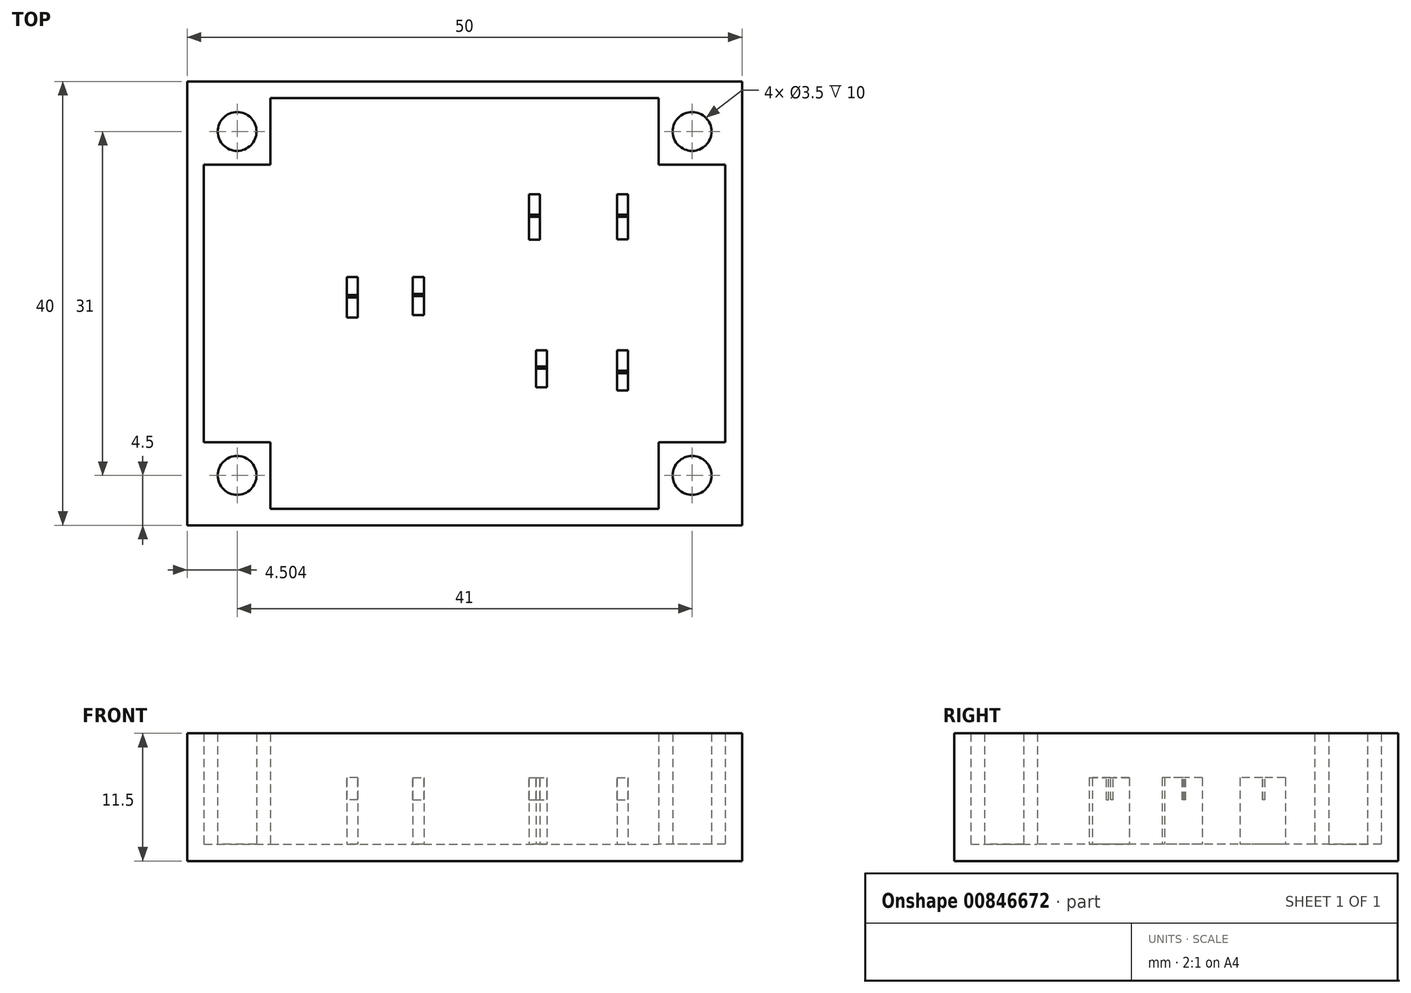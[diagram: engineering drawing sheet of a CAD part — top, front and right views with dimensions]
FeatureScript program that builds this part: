
annotation { "Feature Type Name" : "Feature", "Feature Type Description" : "" }
export const myFeature = defineFeature(function(context is Context, id is Id, definition is map)
    precondition{}
    {
        {
            var Q0;
            Q0=qCreatedBy(makeId("Top.planeOp"),FACE);
            var sketch = newSketch(context, id + "F0", { "sketchPlane" : qUnion([Q0])});
            skLineSegment(sketch, "E0.bottom", {"start": v(-23.35, 9.23) * mm, "end": v(26.65, 9.23) * mm});
            skLineSegment(sketch, "E0.top", {"start": v(-23.35, -30.77) * mm, "end": v(26.65, -30.77) * mm});
            skLineSegment(sketch, "E0.left", {"start": v(-23.35, 9.23) * mm, "end": v(-23.35, -30.77) * mm});
            skLineSegment(sketch, "E0.right", {"start": v(26.65, 9.23) * mm, "end": v(26.65, -30.77) * mm});
            skSolve(sketch);
        }
        {
            var Q0;
            Q0=makeQuery(id+"F0.imprint","IMPRINT",FACE,{"disambiguationData":[TD([[makeQuery(id+"F0.imprint","IMPRINT",EDGE,{"derivedFrom":sQuery(id+"F0.wireOp",EDGE,"E0.bottom")}),-1.0]])]});
            extrude(context, id + "F1", {"entities" : qUnion([Q0]), "depth" : 1.5 * mm, "offsetDistance" : 25 * mm});
        }
        {
            var Q0;
            Q0=makeQuery(id+"F1.opExtrude","CAP_FACE",FACE,{"disambiguationData":[OSD([sQuery(id+"F0.wireOp",EDGE,"E0.bottom"),sQuery(id+"F0.wireOp",EDGE,"E0.top"),sQuery(id+"F0.wireOp",EDGE,"E0.left"),sQuery(id+"F0.wireOp",EDGE,"E0.right")])],"isStart":false});
            var sketch = newSketch(context, id + "F2", { "sketchPlane" : qUnion([Q0])});
            skLineSegment(sketch, "E1.bottom", {"start": v(-23.35, 9.23) * mm, "end": v(26.65, 9.23) * mm});
            skLineSegment(sketch, "E1.top", {"start": v(-23.35, -30.77) * mm, "end": v(26.65, -30.77) * mm});
            skLineSegment(sketch, "E1.left", {"start": v(-23.35, 9.23) * mm, "end": v(-23.35, -30.77) * mm});
            skLineSegment(sketch, "E1.right", {"start": v(26.65, 9.23) * mm, "end": v(26.65, -30.77) * mm});
            skLineSegment(sketch, "E2.bottom", {"start": v(-21.85, 7.73) * mm, "end": v(25.15, 7.73) * mm});
            skLineSegment(sketch, "E2.top", {"start": v(-21.85, -29.27) * mm, "end": v(25.15, -29.27) * mm});
            skLineSegment(sketch, "E2.left", {"start": v(-21.85, 7.73) * mm, "end": v(-21.85, -29.27) * mm});
            skLineSegment(sketch, "E2.right", {"start": v(25.15, 7.73) * mm, "end": v(25.15, -29.27) * mm});
            skLineSegment(sketch, "E3.bottom", {"start": v(19.15, 7.73) * mm, "end": v(25.15, 7.73) * mm});
            skLineSegment(sketch, "E3.top", {"start": v(19.15, 1.73) * mm, "end": v(25.15, 1.73) * mm});
            skLineSegment(sketch, "E3.left", {"start": v(19.15, 7.73) * mm, "end": v(19.15, 1.73) * mm});
            skLineSegment(sketch, "E3.right", {"start": v(25.15, 7.73) * mm, "end": v(25.15, 1.73) * mm});
            skCircle(sketch, "E4", {"center": v(22.29, 4.73) * mm, "radius": 1.75 * mm});
            skPoint(sketch, "E4.centerSnap0", {"position": v(25.15, 4.73) * mm});
            skSolve(sketch);
        }
        {
            var Q0;
            Q0 = qSketchRegion(id + "F2", true);
            extrude(context, id + "F3", {"entities" : qUnion([Q0]), "operationType" : NewBodyOperationType.ADD, "depth" : 10 * mm, "offsetDistance" : 25 * mm});
        }
        {
            var Q0;
            Q0=makeQuery(id+"F1.opExtrude","CAP_FACE",FACE,{"disambiguationData":[OSD([sQuery(id+"F0.wireOp",EDGE,"E0.bottom"),sQuery(id+"F0.wireOp",EDGE,"E0.top"),sQuery(id+"F0.wireOp",EDGE,"E0.left"),sQuery(id+"F0.wireOp",EDGE,"E0.right")])],"isStart":false});
            var sketch = newSketch(context, id + "F4", { "sketchPlane" : qUnion([Q0])});
            skLineSegment(sketch, "E5.bottom", {"start": v(-21.85, 7.73) * mm, "end": v(-15.85, 7.73) * mm});
            skLineSegment(sketch, "E5.top", {"start": v(-21.85, 1.73) * mm, "end": v(-15.85, 1.73) * mm});
            skLineSegment(sketch, "E5.left", {"start": v(-21.85, 7.73) * mm, "end": v(-21.85, 1.73) * mm});
            skLineSegment(sketch, "E5.right", {"start": v(-15.85, 7.73) * mm, "end": v(-15.85, 1.73) * mm});
            skLineSegment(sketch, "E6", {"start": v(-21.85, 1.73) * mm, "end": v(-15.85, 7.73) * mm});
            skLineSegment(sketch, "E7", {"start": v(-21.85, 7.73) * mm, "end": v(-15.85, 1.73) * mm});
            skCircle(sketch, "E8", {"center": v(-18.85, 4.73) * mm, "radius": 1.75 * mm});
            skSolve(sketch);
        }
        {
            var Q0;
            Q0 = qSketchRegion(id + "F4", true);
            extrude(context, id + "F5", {"entities" : qUnion([Q0]), "operationType" : NewBodyOperationType.ADD, "depth" : 10 * mm, "offsetDistance" : 25 * mm});
        }
        {
            var Q0;
            Q0=makeQuery(id+"F5.boolean.opBoolean","SPLIT",FACE,{"disambiguationData":[TD([makeQuery(id+"F3.opExtrude","SWEPT_FACE",FACE,{"disambiguationData":[OSD([sQuery(id+"F2.wireOp",EDGE,"E2.top")])]})])],"derivedFrom":makeQuery(id+"F1.opExtrude","CAP_FACE",FACE,{"disambiguationData":[OSD([sQuery(id+"F0.wireOp",EDGE,"E0.bottom"),sQuery(id+"F0.wireOp",EDGE,"E0.top"),sQuery(id+"F0.wireOp",EDGE,"E0.left"),sQuery(id+"F0.wireOp",EDGE,"E0.right")])],"isStart":false})});
            var sketch = newSketch(context, id + "F6", { "sketchPlane" : qUnion([Q0])});
            skLineSegment(sketch, "E9.bottom", {"start": v(-21.85, -29.27) * mm, "end": v(-15.85, -29.27) * mm});
            skLineSegment(sketch, "E9.top", {"start": v(-21.85, -23.27) * mm, "end": v(-15.85, -23.27) * mm});
            skLineSegment(sketch, "E9.left", {"start": v(-21.85, -29.27) * mm, "end": v(-21.85, -23.27) * mm});
            skLineSegment(sketch, "E9.right", {"start": v(-15.85, -29.27) * mm, "end": v(-15.85, -23.27) * mm});
            skLineSegment(sketch, "E10", {"start": v(-21.85, -29.27) * mm, "end": v(-15.85, -23.27) * mm});
            skLineSegment(sketch, "E11", {"start": v(-21.85, -23.27) * mm, "end": v(-15.85, -29.27) * mm});
            skCircle(sketch, "E12", {"center": v(-18.85, -26.27) * mm, "radius": 1.75 * mm});
            skSolve(sketch);
        }
        {
            var Q0;
            Q0 = qSketchRegion(id + "F6", true);
            extrude(context, id + "F7", {"entities" : qUnion([Q0]), "operationType" : NewBodyOperationType.ADD, "depth" : 10 * mm, "offsetDistance" : 25 * mm});
        }
        {
            var Q0;
            {var subQ3=makeQuery(id+"F3.opExtrude","SWEPT_FACE",FACE,{"disambiguationData":[OSD([sQuery(id+"F2.wireOp",EDGE,"E2.top")])]});Q0=makeQuery(id+"F7.boolean.opBoolean","SPLIT",FACE,{"disambiguationData":[TD([subQ3])],"derivedFrom":makeQuery(id+"F5.boolean.opBoolean","SPLIT",FACE,{"disambiguationData":[TD([subQ3])],"derivedFrom":makeQuery(id+"F1.opExtrude","CAP_FACE",FACE,{"disambiguationData":[OSD([sQuery(id+"F0.wireOp",EDGE,"E0.bottom"),sQuery(id+"F0.wireOp",EDGE,"E0.top"),sQuery(id+"F0.wireOp",EDGE,"E0.left"),sQuery(id+"F0.wireOp",EDGE,"E0.right")])],"isStart":false})})});}
            var sketch = newSketch(context, id + "F8", { "sketchPlane" : qUnion([Q0])});
            skLineSegment(sketch, "E13.bottom", {"start": v(25.15, 7.73) * mm, "end": v(19.15, 7.73) * mm});
            skLineSegment(sketch, "E13.top", {"start": v(25.15, 1.73) * mm, "end": v(19.15, 1.73) * mm});
            skLineSegment(sketch, "E13.left", {"start": v(25.15, 7.73) * mm, "end": v(25.15, 1.73) * mm});
            skLineSegment(sketch, "E13.right", {"start": v(19.15, 7.73) * mm, "end": v(19.15, 1.73) * mm});
            skLineSegment(sketch, "E14", {"start": v(19.15, 1.73) * mm, "end": v(25.15, 7.73) * mm});
            skLineSegment(sketch, "E15", {"start": v(19.15, 7.73) * mm, "end": v(25.15, 1.73) * mm});
            skCircle(sketch, "E16", {"center": v(22.15, 4.73) * mm, "radius": 1.75 * mm});
            skSolve(sketch);
        }
        {
            var Q0;
            Q0 = qSketchRegion(id + "F8", true);
            extrude(context, id + "F9", {"entities" : qUnion([Q0]), "operationType" : NewBodyOperationType.ADD, "depth" : 10 * mm, "offsetDistance" : 25 * mm});
        }
        {
            var Q0;
            {var subQ3=makeQuery(id+"F3.opExtrude","SWEPT_FACE",FACE,{"disambiguationData":[OSD([sQuery(id+"F2.wireOp",EDGE,"E2.top")])]});Q0=makeQuery(id+"F9.boolean.opBoolean","SPLIT",FACE,{"disambiguationData":[TD([subQ3])],"derivedFrom":makeQuery(id+"F7.boolean.opBoolean","SPLIT",FACE,{"disambiguationData":[TD([subQ3])],"derivedFrom":makeQuery(id+"F5.boolean.opBoolean","SPLIT",FACE,{"disambiguationData":[TD([subQ3])],"derivedFrom":makeQuery(id+"F1.opExtrude","CAP_FACE",FACE,{"disambiguationData":[OSD([sQuery(id+"F0.wireOp",EDGE,"E0.bottom"),sQuery(id+"F0.wireOp",EDGE,"E0.top"),sQuery(id+"F0.wireOp",EDGE,"E0.left"),sQuery(id+"F0.wireOp",EDGE,"E0.right")])],"isStart":false})})})});}
            var sketch = newSketch(context, id + "F10", { "sketchPlane" : qUnion([Q0])});
            skLineSegment(sketch, "E17.bottom", {"start": v(25.15, -29.27) * mm, "end": v(19.15, -29.27) * mm});
            skLineSegment(sketch, "E17.top", {"start": v(25.15, -23.27) * mm, "end": v(19.15, -23.27) * mm});
            skLineSegment(sketch, "E17.left", {"start": v(25.15, -29.27) * mm, "end": v(25.15, -23.27) * mm});
            skLineSegment(sketch, "E17.right", {"start": v(19.15, -29.27) * mm, "end": v(19.15, -23.27) * mm});
            skLineSegment(sketch, "E18", {"start": v(19.15, -29.27) * mm, "end": v(25.15, -23.27) * mm});
            skLineSegment(sketch, "E19", {"start": v(19.15, -23.27) * mm, "end": v(25.15, -29.27) * mm});
            skCircle(sketch, "E20", {"center": v(22.15, -26.27) * mm, "radius": 1.75 * mm});
            skSolve(sketch);
        }
        {
            var Q0;
            Q0 = qSketchRegion(id + "F10", true);
            extrude(context, id + "F11", {"entities" : qUnion([Q0]), "operationType" : NewBodyOperationType.ADD, "depth" : 10 * mm, "offsetDistance" : 25 * mm});
        }
        {
            var Q0;
            Q0=makeQuery(id+"F1.opExtrude","SWEPT_BODY",BODY,{"disambiguationData":[OSD([sQuery(id+"F0.wireOp",EDGE,"E0.bottom"),sQuery(id+"F0.wireOp",EDGE,"E0.top"),sQuery(id+"F0.wireOp",EDGE,"E0.left"),sQuery(id+"F0.wireOp",EDGE,"E0.right")])]});
            transform(context, id + "F12", {"entities" : qUnion([Q0]), "transformType" : TransformType.TRANSLATION_3D, "dx" : 0 * mm, "dy" : 0 * mm, "dz" : 0 * mm, "makeCopy" : true});
        }
        {
            var Q0;
            Q0=makeQuery(id+"F12.opPattern","COPY",BODY,{"derivedFrom":makeQuery(id+"F1.opExtrude","SWEPT_BODY",BODY,{"disambiguationData":[OSD([sQuery(id+"F0.wireOp",EDGE,"E0.bottom"),sQuery(id+"F0.wireOp",EDGE,"E0.top"),sQuery(id+"F0.wireOp",EDGE,"E0.left"),sQuery(id+"F0.wireOp",EDGE,"E0.right")])]}),"instanceName":"1"});
            deleteBodies(context, id + "F13", {"entities" : qUnion([Q0])});
        }
        {
            var Q0;
            {var subQ6=makeQuery(id+"F3.opExtrude","SWEPT_FACE",FACE,{"disambiguationData":[OSD([sQuery(id+"F2.wireOp",EDGE,"E2.top")])]});Q0=makeQuery(id+"F11.boolean.opBoolean","SPLIT",FACE,{"disambiguationData":[TD([subQ6])],"derivedFrom":makeQuery(id+"F9.boolean.opBoolean","SPLIT",FACE,{"disambiguationData":[TD([subQ6])],"derivedFrom":makeQuery(id+"F7.boolean.opBoolean","SPLIT",FACE,{"disambiguationData":[TD([subQ6])],"derivedFrom":makeQuery(id+"F5.boolean.opBoolean","SPLIT",FACE,{"disambiguationData":[TD([subQ6])],"derivedFrom":makeQuery(id+"F1.opExtrude","CAP_FACE",FACE,{"disambiguationData":[OSD([sQuery(id+"F0.wireOp",EDGE,"E0.bottom"),sQuery(id+"F0.wireOp",EDGE,"E0.top"),sQuery(id+"F0.wireOp",EDGE,"E0.left"),sQuery(id+"F0.wireOp",EDGE,"E0.right")])],"isStart":false})})})})});}
            var sketch = newSketch(context, id + "F14", { "sketchPlane" : qUnion([Q0])});
            skLineSegment(sketch, "E21.bottom", {"start": v(16.38, -0.92) * mm, "end": v(15.38, -0.92) * mm});
            skLineSegment(sketch, "E21.top", {"start": v(16.38, -5) * mm, "end": v(15.38, -5) * mm});
            skLineSegment(sketch, "E21.left", {"start": v(16.38, -0.92) * mm, "end": v(16.38, -5) * mm});
            skLineSegment(sketch, "E21.right", {"start": v(15.38, -0.92) * mm, "end": v(15.38, -5) * mm});
            skSolve(sketch);
        }
        {
            var Q0;
            Q0 = qSketchRegion(id + "F14", true);
            extrude(context, id + "F15", {"entities" : qUnion([Q0]), "operationType" : NewBodyOperationType.ADD, "depth" : 6 * mm, "offsetDistance" : 25 * mm});
        }
        {
            var Q0;
            Q0=makeQuery(id+"F15.opExtrude","CAP_FACE",FACE,{"disambiguationData":[OSD([sQuery(id+"F14.wireOp",EDGE,"E21.bottom"),sQuery(id+"F14.wireOp",EDGE,"E21.top"),sQuery(id+"F14.wireOp",EDGE,"E21.left"),sQuery(id+"F14.wireOp",EDGE,"E21.right")])],"isStart":false});
            var sketch = newSketch(context, id + "F16", { "sketchPlane" : qUnion([Q0])});
            skLineSegment(sketch, "E22.bottom", {"start": v(15.38, -2.76) * mm, "end": v(16.38, -2.76) * mm});
            skLineSegment(sketch, "E22.top", {"start": v(15.38, -2.96) * mm, "end": v(16.38, -2.96) * mm});
            skLineSegment(sketch, "E22.left", {"start": v(15.38, -2.76) * mm, "end": v(15.38, -2.96) * mm});
            skLineSegment(sketch, "E22.right", {"start": v(16.38, -2.76) * mm, "end": v(16.38, -2.96) * mm});
            skSolve(sketch);
        }
        {
            var Q0;
            Q0 = qSketchRegion(id + "F16", true);
            extrude(context, id + "F17", {"entities" : qUnion([Q0]), "operationType" : NewBodyOperationType.REMOVE, "oppositeDirection" : true, "depth" : 2 * mm, "offsetDistance" : 25 * mm});
        }
        {
            var Q0;
            {var subQ6=makeQuery(id+"F3.opExtrude","SWEPT_FACE",FACE,{"disambiguationData":[OSD([sQuery(id+"F2.wireOp",EDGE,"E2.top")])]});Q0=makeQuery(id+"F11.boolean.opBoolean","SPLIT",FACE,{"disambiguationData":[TD([subQ6])],"derivedFrom":makeQuery(id+"F9.boolean.opBoolean","SPLIT",FACE,{"disambiguationData":[TD([subQ6])],"derivedFrom":makeQuery(id+"F7.boolean.opBoolean","SPLIT",FACE,{"disambiguationData":[TD([subQ6])],"derivedFrom":makeQuery(id+"F5.boolean.opBoolean","SPLIT",FACE,{"disambiguationData":[TD([subQ6])],"derivedFrom":makeQuery(id+"F1.opExtrude","CAP_FACE",FACE,{"disambiguationData":[OSD([sQuery(id+"F0.wireOp",EDGE,"E0.bottom"),sQuery(id+"F0.wireOp",EDGE,"E0.top"),sQuery(id+"F0.wireOp",EDGE,"E0.left"),sQuery(id+"F0.wireOp",EDGE,"E0.right")])],"isStart":false})})})})});}
            var sketch = newSketch(context, id + "F18", { "sketchPlane" : qUnion([Q0])});
            skLineSegment(sketch, "E23.bottom", {"start": v(15.38, -18.6) * mm, "end": v(16.38, -18.6) * mm});
            skLineSegment(sketch, "E23.top", {"start": v(15.38, -15) * mm, "end": v(16.38, -15) * mm});
            skLineSegment(sketch, "E23.left", {"start": v(15.38, -18.6) * mm, "end": v(15.38, -15) * mm});
            skLineSegment(sketch, "E23.right", {"start": v(16.38, -18.6) * mm, "end": v(16.38, -15) * mm});
            skSolve(sketch);
        }
        {
            var Q0;
            Q0 = qSketchRegion(id + "F18", true);
            extrude(context, id + "F19", {"entities" : qUnion([Q0]), "operationType" : NewBodyOperationType.ADD, "depth" : 6 * mm, "offsetDistance" : 25 * mm});
        }
        {
            var Q0;
            Q0=makeQuery(id+"F19.opExtrude","CAP_FACE",FACE,{"disambiguationData":[OSD([sQuery(id+"F18.wireOp",EDGE,"E23.bottom"),sQuery(id+"F18.wireOp",EDGE,"E23.top"),sQuery(id+"F18.wireOp",EDGE,"E23.left"),sQuery(id+"F18.wireOp",EDGE,"E23.right")])],"isStart":false});
            var sketch = newSketch(context, id + "F20", { "sketchPlane" : qUnion([Q0])});
            skLineSegment(sketch, "E24.bottom", {"start": v(15.38, -16.85) * mm, "end": v(16.38, -16.85) * mm});
            skLineSegment(sketch, "E24.top", {"start": v(15.38, -17.05) * mm, "end": v(16.38, -17.05) * mm});
            skLineSegment(sketch, "E24.left", {"start": v(15.38, -16.85) * mm, "end": v(15.38, -17.05) * mm});
            skLineSegment(sketch, "E24.right", {"start": v(16.38, -16.85) * mm, "end": v(16.38, -17.05) * mm});
            skSolve(sketch);
        }
        {
            var Q0;
            Q0 = qSketchRegion(id + "F20", true);
            extrude(context, id + "F21", {"entities" : qUnion([Q0]), "operationType" : NewBodyOperationType.REMOVE, "oppositeDirection" : true, "depth" : 2 * mm, "offsetDistance" : 25 * mm});
        }
        {
            var Q0;
            {var subQ6=makeQuery(id+"F3.opExtrude","SWEPT_FACE",FACE,{"disambiguationData":[OSD([sQuery(id+"F2.wireOp",EDGE,"E2.top")])]});Q0=makeQuery(id+"F11.boolean.opBoolean","SPLIT",FACE,{"disambiguationData":[TD([subQ6])],"derivedFrom":makeQuery(id+"F9.boolean.opBoolean","SPLIT",FACE,{"disambiguationData":[TD([subQ6])],"derivedFrom":makeQuery(id+"F7.boolean.opBoolean","SPLIT",FACE,{"disambiguationData":[TD([subQ6])],"derivedFrom":makeQuery(id+"F5.boolean.opBoolean","SPLIT",FACE,{"disambiguationData":[TD([subQ6])],"derivedFrom":makeQuery(id+"F1.opExtrude","CAP_FACE",FACE,{"disambiguationData":[OSD([sQuery(id+"F0.wireOp",EDGE,"E0.bottom"),sQuery(id+"F0.wireOp",EDGE,"E0.top"),sQuery(id+"F0.wireOp",EDGE,"E0.left"),sQuery(id+"F0.wireOp",EDGE,"E0.right")])],"isStart":false})})})})});}
            var sketch = newSketch(context, id + "F22", { "sketchPlane" : qUnion([Q0])});
            skLineSegment(sketch, "E25.bottom", {"start": v(8.46, -0.92) * mm, "end": v(7.46, -0.92) * mm});
            skLineSegment(sketch, "E25.top", {"start": v(8.46, -5.01) * mm, "end": v(7.46, -5.01) * mm});
            skLineSegment(sketch, "E25.left", {"start": v(8.46, -0.92) * mm, "end": v(8.46, -5.01) * mm});
            skLineSegment(sketch, "E25.right", {"start": v(7.46, -0.92) * mm, "end": v(7.46, -5.01) * mm});
            skSolve(sketch);
        }
        {
            var Q0;
            Q0 = qSketchRegion(id + "F22", true);
            extrude(context, id + "F23", {"entities" : qUnion([Q0]), "operationType" : NewBodyOperationType.ADD, "depth" : 6 * mm, "offsetDistance" : 25 * mm});
        }
        {
            var Q0;
            Q0=makeQuery(id+"F23.opExtrude","CAP_FACE",FACE,{"disambiguationData":[OSD([sQuery(id+"F22.wireOp",EDGE,"E25.bottom"),sQuery(id+"F22.wireOp",EDGE,"E25.top"),sQuery(id+"F22.wireOp",EDGE,"E25.left"),sQuery(id+"F22.wireOp",EDGE,"E25.right")])],"isStart":false});
            var sketch = newSketch(context, id + "F24", { "sketchPlane" : qUnion([Q0])});
            skLineSegment(sketch, "E26.bottom", {"start": v(7.46, -2.77) * mm, "end": v(8.46, -2.77) * mm});
            skLineSegment(sketch, "E26.top", {"start": v(7.46, -2.97) * mm, "end": v(8.46, -2.97) * mm});
            skLineSegment(sketch, "E26.left", {"start": v(7.46, -2.77) * mm, "end": v(7.46, -2.97) * mm});
            skLineSegment(sketch, "E26.right", {"start": v(8.46, -2.77) * mm, "end": v(8.46, -2.97) * mm});
            skSolve(sketch);
        }
        {
            var Q0;
            Q0 = qSketchRegion(id + "F24", true);
            extrude(context, id + "F25", {"entities" : qUnion([Q0]), "operationType" : NewBodyOperationType.REMOVE, "oppositeDirection" : true, "depth" : 2 * mm, "offsetDistance" : 25 * mm});
        }
        {
            var Q0;
            {var subQ6=makeQuery(id+"F3.opExtrude","SWEPT_FACE",FACE,{"disambiguationData":[OSD([sQuery(id+"F2.wireOp",EDGE,"E2.top")])]});Q0=makeQuery(id+"F11.boolean.opBoolean","SPLIT",FACE,{"disambiguationData":[TD([subQ6])],"derivedFrom":makeQuery(id+"F9.boolean.opBoolean","SPLIT",FACE,{"disambiguationData":[TD([subQ6])],"derivedFrom":makeQuery(id+"F7.boolean.opBoolean","SPLIT",FACE,{"disambiguationData":[TD([subQ6])],"derivedFrom":makeQuery(id+"F5.boolean.opBoolean","SPLIT",FACE,{"disambiguationData":[TD([subQ6])],"derivedFrom":makeQuery(id+"F1.opExtrude","CAP_FACE",FACE,{"disambiguationData":[OSD([sQuery(id+"F0.wireOp",EDGE,"E0.bottom"),sQuery(id+"F0.wireOp",EDGE,"E0.top"),sQuery(id+"F0.wireOp",EDGE,"E0.left"),sQuery(id+"F0.wireOp",EDGE,"E0.right")])],"isStart":false})})})})});}
            var sketch = newSketch(context, id + "F26", { "sketchPlane" : qUnion([Q0])});
            skLineSegment(sketch, "E27.bottom", {"start": v(9.08, -15) * mm, "end": v(8.08, -15) * mm});
            skLineSegment(sketch, "E27.top", {"start": v(9.08, -18.32) * mm, "end": v(8.08, -18.32) * mm});
            skLineSegment(sketch, "E27.left", {"start": v(9.08, -15) * mm, "end": v(9.08, -18.32) * mm});
            skLineSegment(sketch, "E27.right", {"start": v(8.08, -15) * mm, "end": v(8.08, -18.32) * mm});
            skSolve(sketch);
        }
        {
            var Q0;
            Q0 = qSketchRegion(id + "F26", true);
            extrude(context, id + "F27", {"entities" : qUnion([Q0]), "operationType" : NewBodyOperationType.ADD, "depth" : 6 * mm, "offsetDistance" : 25 * mm});
        }
        {
            var Q0;
            Q0=makeQuery(id+"F27.opExtrude","CAP_FACE",FACE,{"disambiguationData":[OSD([sQuery(id+"F26.wireOp",EDGE,"E27.bottom"),sQuery(id+"F26.wireOp",EDGE,"E27.top"),sQuery(id+"F26.wireOp",EDGE,"E27.left"),sQuery(id+"F26.wireOp",EDGE,"E27.right")])],"isStart":false});
            var sketch = newSketch(context, id + "F28", { "sketchPlane" : qUnion([Q0])});
            skLineSegment(sketch, "E28.bottom", {"start": v(8.08, -16.46) * mm, "end": v(9.08, -16.46) * mm});
            skLineSegment(sketch, "E28.top", {"start": v(8.08, -16.66) * mm, "end": v(9.08, -16.66) * mm});
            skLineSegment(sketch, "E28.left", {"start": v(8.08, -16.46) * mm, "end": v(8.08, -16.66) * mm});
            skLineSegment(sketch, "E28.right", {"start": v(9.08, -16.46) * mm, "end": v(9.08, -16.66) * mm});
            skSolve(sketch);
        }
        {
            var Q0;
            Q0 = qSketchRegion(id + "F28", true);
            extrude(context, id + "F29", {"entities" : qUnion([Q0]), "operationType" : NewBodyOperationType.REMOVE, "oppositeDirection" : true, "depth" : 2 * mm, "offsetDistance" : 25 * mm});
        }
        {
            var Q0;
            {var subQ6=makeQuery(id+"F3.opExtrude","SWEPT_FACE",FACE,{"disambiguationData":[OSD([sQuery(id+"F2.wireOp",EDGE,"E2.top")])]});Q0=makeQuery(id+"F11.boolean.opBoolean","SPLIT",FACE,{"disambiguationData":[TD([subQ6])],"derivedFrom":makeQuery(id+"F9.boolean.opBoolean","SPLIT",FACE,{"disambiguationData":[TD([subQ6])],"derivedFrom":makeQuery(id+"F7.boolean.opBoolean","SPLIT",FACE,{"disambiguationData":[TD([subQ6])],"derivedFrom":makeQuery(id+"F5.boolean.opBoolean","SPLIT",FACE,{"disambiguationData":[TD([subQ6])],"derivedFrom":makeQuery(id+"F1.opExtrude","CAP_FACE",FACE,{"disambiguationData":[OSD([sQuery(id+"F0.wireOp",EDGE,"E0.bottom"),sQuery(id+"F0.wireOp",EDGE,"E0.top"),sQuery(id+"F0.wireOp",EDGE,"E0.left"),sQuery(id+"F0.wireOp",EDGE,"E0.right")])],"isStart":false})})})})});}
            var sketch = newSketch(context, id + "F30", { "sketchPlane" : qUnion([Q0])});
            skLineSegment(sketch, "E29.bottom", {"start": v(-2.01, -8.4) * mm, "end": v(-3.01, -8.4) * mm});
            skLineSegment(sketch, "E29.top", {"start": v(-2.01, -11.8) * mm, "end": v(-3.01, -11.8) * mm});
            skLineSegment(sketch, "E29.left", {"start": v(-2.01, -8.4) * mm, "end": v(-2.01, -11.8) * mm});
            skLineSegment(sketch, "E29.right", {"start": v(-3.01, -8.4) * mm, "end": v(-3.01, -11.8) * mm});
            skSolve(sketch);
        }
        {
            var Q0;
            Q0 = qSketchRegion(id + "F30", true);
            extrude(context, id + "F31", {"entities" : qUnion([Q0]), "operationType" : NewBodyOperationType.ADD, "depth" : 6 * mm, "offsetDistance" : 25 * mm});
        }
        {
            var Q0;
            Q0=makeQuery(id+"F31.opExtrude","CAP_FACE",FACE,{"disambiguationData":[OSD([sQuery(id+"F30.wireOp",EDGE,"E29.bottom"),sQuery(id+"F30.wireOp",EDGE,"E29.top"),sQuery(id+"F30.wireOp",EDGE,"E29.left"),sQuery(id+"F30.wireOp",EDGE,"E29.right")])],"isStart":false});
            var sketch = newSketch(context, id + "F32", { "sketchPlane" : qUnion([Q0])});
            skLineSegment(sketch, "E30.bottom", {"start": v(-3.01, -9.9) * mm, "end": v(-2.01, -9.9) * mm});
            skLineSegment(sketch, "E30.top", {"start": v(-3.01, -10.1) * mm, "end": v(-2.01, -10.1) * mm});
            skLineSegment(sketch, "E30.left", {"start": v(-3.01, -9.9) * mm, "end": v(-3.01, -10.1) * mm});
            skLineSegment(sketch, "E30.right", {"start": v(-2.01, -9.9) * mm, "end": v(-2.01, -10.1) * mm});
            skSolve(sketch);
        }
        {
            var Q0;
            Q0 = qSketchRegion(id + "F32", true);
            extrude(context, id + "F33", {"entities" : qUnion([Q0]), "operationType" : NewBodyOperationType.REMOVE, "oppositeDirection" : true, "depth" : 2 * mm, "offsetDistance" : 25 * mm});
        }
        {
            var Q0;
            {var subQ6=makeQuery(id+"F3.opExtrude","SWEPT_FACE",FACE,{"disambiguationData":[OSD([sQuery(id+"F2.wireOp",EDGE,"E2.top")])]});Q0=makeQuery(id+"F11.boolean.opBoolean","SPLIT",FACE,{"disambiguationData":[TD([subQ6])],"derivedFrom":makeQuery(id+"F9.boolean.opBoolean","SPLIT",FACE,{"disambiguationData":[TD([subQ6])],"derivedFrom":makeQuery(id+"F7.boolean.opBoolean","SPLIT",FACE,{"disambiguationData":[TD([subQ6])],"derivedFrom":makeQuery(id+"F5.boolean.opBoolean","SPLIT",FACE,{"disambiguationData":[TD([subQ6])],"derivedFrom":makeQuery(id+"F1.opExtrude","CAP_FACE",FACE,{"disambiguationData":[OSD([sQuery(id+"F0.wireOp",EDGE,"E0.bottom"),sQuery(id+"F0.wireOp",EDGE,"E0.top"),sQuery(id+"F0.wireOp",EDGE,"E0.left"),sQuery(id+"F0.wireOp",EDGE,"E0.right")])],"isStart":false})})})})});}
            var sketch = newSketch(context, id + "F34", { "sketchPlane" : qUnion([Q0])});
            skLineSegment(sketch, "E31.bottom", {"start": v(-7.96, -8.4) * mm, "end": v(-8.96, -8.4) * mm});
            skLineSegment(sketch, "E31.top", {"start": v(-7.96, -12.04) * mm, "end": v(-8.96, -12.04) * mm});
            skLineSegment(sketch, "E31.left", {"start": v(-7.96, -8.4) * mm, "end": v(-7.96, -12.04) * mm});
            skLineSegment(sketch, "E31.right", {"start": v(-8.96, -8.4) * mm, "end": v(-8.96, -12.04) * mm});
            skSolve(sketch);
        }
        {
            var Q0;
            Q0 = qSketchRegion(id + "F34", true);
            extrude(context, id + "F35", {"entities" : qUnion([Q0]), "operationType" : NewBodyOperationType.ADD, "depth" : 6 * mm, "offsetDistance" : 25 * mm});
        }
        {
            var Q0;
            Q0=makeQuery(id+"F35.opExtrude","CAP_FACE",FACE,{"disambiguationData":[OSD([sQuery(id+"F34.wireOp",EDGE,"E31.bottom"),sQuery(id+"F34.wireOp",EDGE,"E31.top"),sQuery(id+"F34.wireOp",EDGE,"E31.left"),sQuery(id+"F34.wireOp",EDGE,"E31.right")])],"isStart":false});
            var sketch = newSketch(context, id + "F36", { "sketchPlane" : qUnion([Q0])});
            skLineSegment(sketch, "E32.bottom", {"start": v(-7.96, -10.22) * mm, "end": v(-8.96, -10.22) * mm});
            skLineSegment(sketch, "E32.top", {"start": v(-7.96, -10.02) * mm, "end": v(-8.96, -10.02) * mm});
            skLineSegment(sketch, "E32.left", {"start": v(-7.96, -10.22) * mm, "end": v(-7.96, -10.02) * mm});
            skLineSegment(sketch, "E32.right", {"start": v(-8.96, -10.22) * mm, "end": v(-8.96, -10.02) * mm});
            skSolve(sketch);
        }
        {
            var Q0;
            Q0 = qSketchRegion(id + "F36", true);
            extrude(context, id + "F37", {"entities" : qUnion([Q0]), "operationType" : NewBodyOperationType.REMOVE, "oppositeDirection" : true, "depth" : 2 * mm, "offsetDistance" : 25 * mm});
        }
    });
